# Revit family: Abmessungen MDA
name_source: partatom
category: Air Terminals
revit_build: Autodesk Revit 2017 (Build: 20160225_1515(x64)
units: mm (PartAtom-declared; Revit-internal decimal feet)

## family parameters
Always vertical = Yes
Cut with Voids When Loaded = No
Part Type = Normal
Room Calculation Point = No
Round Connector Dimension = Use Diameter
Shared = No
Work Plane-Based = No

## types (3) — shared parameters
Max Flow = 0.0 L/s
Min Flow = 0.0 L/s
Pressure Drop = 0.0 Pa

## per-type parameters (varying)
| type | A | B | DN | H | Index |
| MDA 250 | 250 mm  [stored 0.82021 ft] | 300 mm | 100 mm  [stored 0.328084 ft] | 35 mm | 1 |
| MDA 315 | 315 mm  [stored 1.03346 ft] | 365 mm  [stored 1.19751 ft] | 125 mm  [stored 0.410105 ft] | 39 mm | 2 |
| MDA 400 | 400 mm  [stored 1.31234 ft] | 450 mm  [stored 1.47638 ft] | 160 mm  [stored 0.524934 ft] | 44 mm | 3 |

note: [stored X ft] marks values corroborated as IEEE doubles in the binary element streams (Revit-internal decimal feet)

## geometry (parser evidence)
native form markers: Sweep x15
no freeform markers — native parametric forms only
